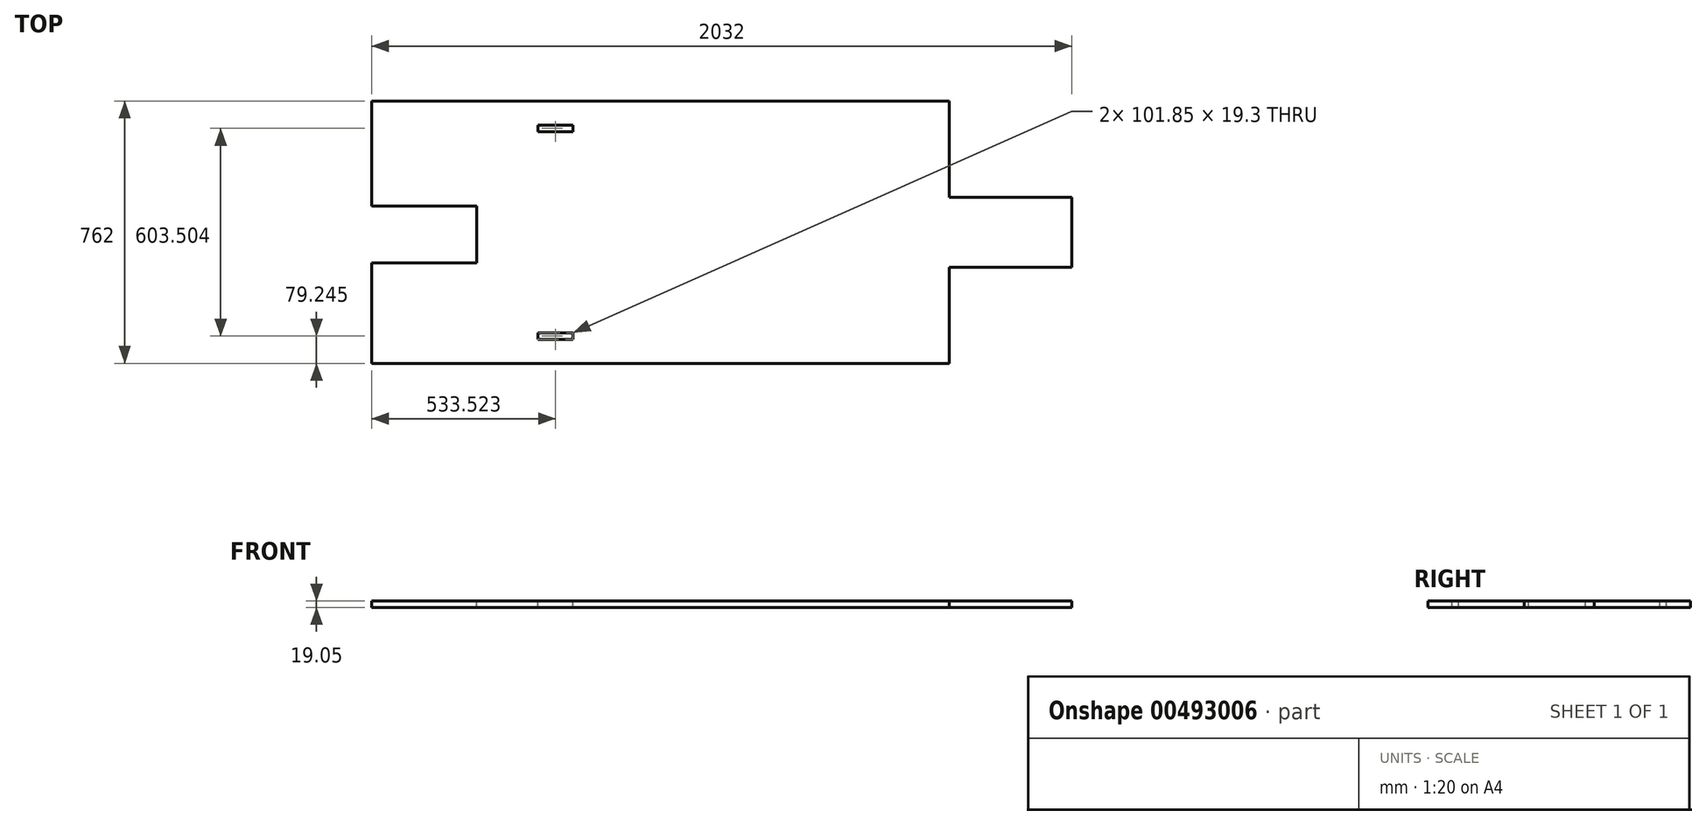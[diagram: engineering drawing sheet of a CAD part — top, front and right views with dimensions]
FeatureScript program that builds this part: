
annotation { "Feature Type Name" : "Feature", "Feature Type Description" : "" }
export const myFeature = defineFeature(function(context is Context, id is Id, definition is map)
    precondition{}
    {
        {
            var Q0;
            Q0=qCreatedBy(makeId("Top.planeOp"),FACE);
            var sketch = newSketch(context, id + "F0", { "sketchPlane" : qUnion([Q0])});
            skLineSegment(sketch, "E0", {"start": v(-69.3, -150.08) * mm, "end": v(-69.3, 611.92) * mm});
            skLineSegment(sketch, "E1", {"start": v(-69.3, -150.08) * mm, "end": v(1607.1, -150.08) * mm});
            skLineSegment(sketch, "E2", {"start": v(-69.3, 611.92) * mm, "end": v(-69.3, 0) * mm});
            skLineSegment(sketch, "E3", {"start": v(1607.1, 129.32) * mm, "end": v(1962.7, 129.32) * mm});
            skLineSegment(sketch, "E4", {"start": v(1962.7, 129.32) * mm, "end": v(1962.7, 332.52) * mm});
            skLineSegment(sketch, "E5", {"start": v(1962.7, 332.52) * mm, "end": v(1607.1, 332.52) * mm});
            skLineSegment(sketch, "E6", {"start": v(-69.3, 611.92) * mm, "end": v(1607.1, 611.92) * mm});
            skLineSegment(sketch, "E7", {"start": v(1607.1, 332.52) * mm, "end": v(1607.1, 611.92) * mm});
            skLineSegment(sketch, "E8", {"start": v(1607.1, 129.32) * mm, "end": v(1607.1, -150.08) * mm});
            skSolve(sketch);
        }
        {
            var Q0;
            Q0=makeQuery(id+"F0.imprint","IMPRINT",FACE,{"disambiguationData":[TD([[makeQuery(id+"F0.imprint","IMPRINT",EDGE,{"derivedFrom":sQuery(id+"F0.wireOp",EDGE,"E0")}),-1.0]])]});
            var Q1;
            {var subQ0=sQuery(id+"F0.wireOp",EDGE,"uOlpoSCx-nx6F-U7As-y7WT-7i0BQtRs1I8v");Q1=makeQuery(id+"F0.imprint","IMPRINT",FACE,{"disambiguationData":[TD([[makeQuery(id+"F0.imprint","IMPRINT",EDGE,{"derivedFrom":subQ0}),1.0]])]});}
            var Q2;
            {var subQ0=sQuery(id+"F0.wireOp",EDGE,"E3");Q2=makeQuery(id+"F0.imprint","IMPRINT",FACE,{"disambiguationData":[TD([[makeQuery(id+"F0.imprint","IMPRINT",EDGE,{"derivedFrom":subQ0}),1.0]])]});}
            extrude(context, id + "F1", {"entities" : qUnion([Q0, Q1, Q2]), "depth" : 19.05 * mm, "offsetDistance" : 25.4 * mm});
        }
        {
            var Q0;
            Q0=makeQuery(id+"F1.opExtrude","CAP_FACE",FACE,{"disambiguationData":[OSD([sQuery(id+"F0.wireOp",EDGE,"E0"),sQuery(id+"F0.wireOp",EDGE,"E1"),sQuery(id+"F0.wireOp",EDGE,"x0LycHuI-RLPF-VvZt-5vee-dlD6wOmq47J5"),sQuery(id+"F0.wireOp",EDGE,"OcUdmKXy-iof9-d5ew-JIiK-O5hlHMasW4m4"),sQuery(id+"F0.wireOp",EDGE,"2tRLnRk0-2LWo-bkda-5gZi-ShlIWcicLbl6"),sQuery(id+"F0.wireOp",EDGE,"uOlpoSCx-nx6F-U7As-y7WT-7i0BQtRs1I8v"),sQuery(id+"F0.wireOp",EDGE,"bJd0vNHp-mW39-6Gpc-BYpA-SkmNAsCOj4YE"),sQuery(id+"F0.wireOp",EDGE,"nPw6lrbQ-a9Zl-HGWJ-en7K-Fit0Y6SgKsxy"),sQuery(id+"F0.wireOp",EDGE,"E2")])],"isStart":false});
            var sketch = newSketch(context, id + "F2", { "sketchPlane" : qUnion([Q0])});
            skLineSegment(sketch, "E9", {"start": v(-69.3, 611.92) * mm, "end": v(-69.3, 643.92) * mm});
            skLineSegment(sketch, "E10", {"start": v(-69.3, 643.92) * mm, "end": v(387.9, 643.92) * mm});
            skLineSegment(sketch, "E11", {"start": v(387.9, 643.92) * mm, "end": v(387.9, 542.32) * mm});
            skLineSegment(sketch, "E12.bottom", {"start": v(515.15, 542.32) * mm, "end": v(413.3, 542.32) * mm});
            skLineSegment(sketch, "E12.top", {"start": v(515.15, 523.02) * mm, "end": v(413.3, 523.02) * mm});
            skLineSegment(sketch, "E12.left", {"start": v(515.15, 542.32) * mm, "end": v(515.15, 523.02) * mm});
            skLineSegment(sketch, "E12.right", {"start": v(413.3, 542.32) * mm, "end": v(413.3, 523.02) * mm});
            skLineSegment(sketch, "E13.MirrorCS", {"start": v(515.15, -80.49) * mm, "end": v(515.15, -61.18) * mm});
            skLineSegment(sketch, "E14.MirrorCS", {"start": v(413.3, -80.49) * mm, "end": v(413.3, -61.18) * mm});
            skLineSegment(sketch, "E15.MirrorCS", {"start": v(515.15, -80.49) * mm, "end": v(413.3, -80.49) * mm});
            skLineSegment(sketch, "E16.MirrorCS", {"start": v(515.15, -61.18) * mm, "end": v(413.3, -61.18) * mm});
            skLineSegment(sketch, "E17", {"start": v(413.3, 523.02) * mm, "end": v(413.3, 230.92) * mm});
            skLineSegment(sketch, "E18", {"start": v(413.3, -80.49) * mm, "end": v(235.5, -80.49) * mm});
            skLineSegment(sketch, "E19", {"start": v(413.3, 542.32) * mm, "end": v(-69.3, 542.32) * mm});
            skLineSegment(sketch, "E20", {"start": v(-69.3, 224.8) * mm, "end": v(-69.3, 307.35) * mm});
            skLineSegment(sketch, "E21", {"start": v(-69.3, 224.8) * mm, "end": v(-69.3, 142.25) * mm});
            skLineSegment(sketch, "E22", {"start": v(-69.3, 142.25) * mm, "end": v(235.5, 142.25) * mm});
            skLineSegment(sketch, "E23", {"start": v(235.5, 142.25) * mm, "end": v(235.5, 307.35) * mm});
            skLineSegment(sketch, "E24", {"start": v(235.5, 307.35) * mm, "end": v(-69.3, 307.35) * mm});
            skSolve(sketch);
        }
        {
            var Q0;
            Q0 = qSketchRegion(id + "F2", true);
            extrude(context, id + "F3", {"entities" : qUnion([Q0]), "operationType" : NewBodyOperationType.REMOVE, "depth" : -25.4 * mm, "offsetDistance" : 25.4 * mm});
        }
    });
